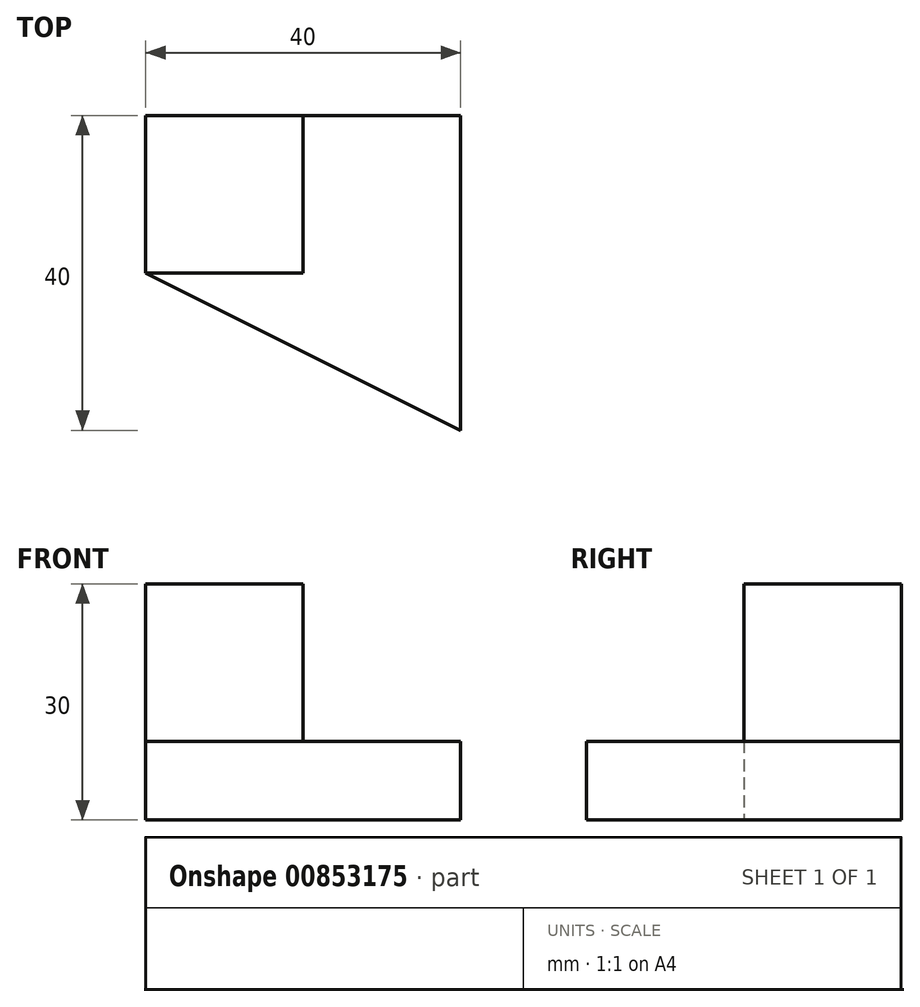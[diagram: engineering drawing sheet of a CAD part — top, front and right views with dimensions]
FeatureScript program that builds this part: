
annotation { "Feature Type Name" : "Feature", "Feature Type Description" : "" }
export const myFeature = defineFeature(function(context is Context, id is Id, definition is map)
    precondition{}
    {
        {
            var Q0;
            Q0=qCreatedBy(makeId("Top.planeOp"),FACE);
            var sketch = newSketch(context, id + "F0", { "sketchPlane" : qUnion([Q0])});
            skLineSegment(sketch, "E0.bottom", {"start": v(0, 0) * mm, "end": v(-20, 0) * mm});
            skLineSegment(sketch, "E0.top", {"start": v(0, 20) * mm, "end": v(-20, 20) * mm});
            skLineSegment(sketch, "E0.left", {"start": v(0, 0) * mm, "end": v(0, 20) * mm});
            skLineSegment(sketch, "E0.right", {"start": v(-20, 0) * mm, "end": v(-20, 20) * mm});
            skLineSegment(sketch, "E1", {"start": v(-20, 20) * mm, "end": v(20, 20) * mm});
            skLineSegment(sketch, "E2", {"start": v(20, 20) * mm, "end": v(20, -20) * mm});
            skLineSegment(sketch, "E3", {"start": v(20, -20) * mm, "end": v(-20, 0) * mm});
            skSolve(sketch);
        }
        {
            var Q0;
            Q0=makeQuery(id+"F0.imprint","IMPRINT",FACE,{"disambiguationData":[TD([[makeQuery(id+"F0.imprint","IMPRINT",EDGE,{"derivedFrom":sQuery(id+"F0.wireOp",EDGE,"E0.bottom")}),-1.0]])]});
            extrude(context, id + "F1", {"entities" : qUnion([Q0]), "depth" : 30 * mm, "offsetDistance" : 25 * mm});
        }
        {
            var Q0;
            Q0=makeQuery(id+"F0.imprint","IMPRINT",FACE,{"disambiguationData":[TD([[makeQuery(id+"F0.imprint","IMPRINT",EDGE,{"derivedFrom":sQuery(id+"F0.wireOp",EDGE,"E0.bottom")}),1.0]])]});
            extrude(context, id + "F2", {"entities" : qUnion([Q0]), "operationType" : NewBodyOperationType.ADD, "depth" : 10 * mm, "offsetDistance" : 25 * mm});
        }
    });
